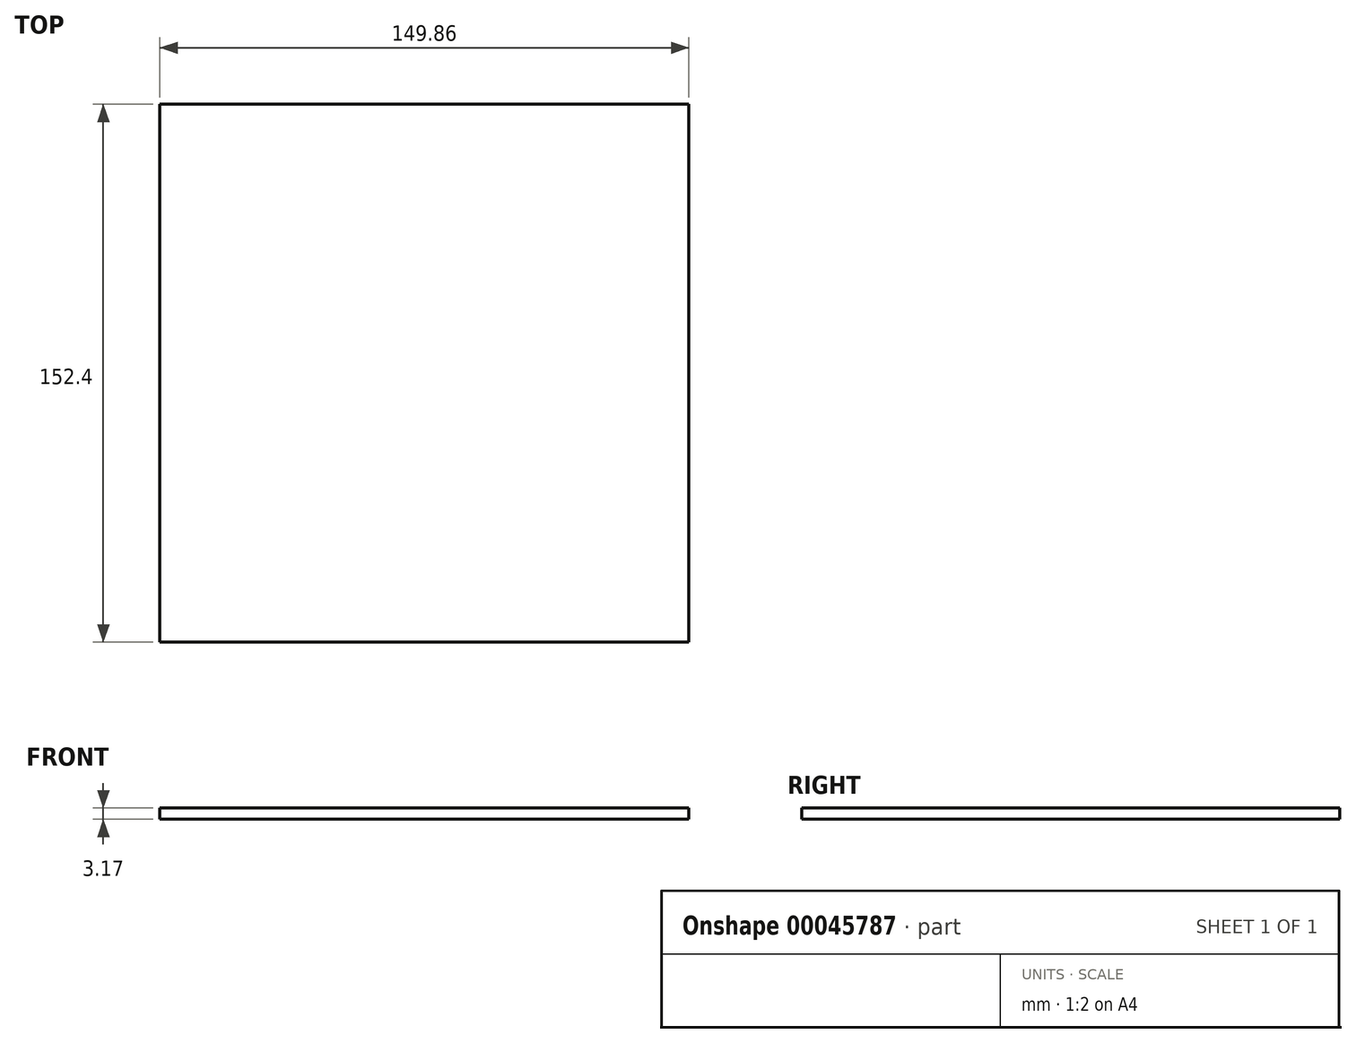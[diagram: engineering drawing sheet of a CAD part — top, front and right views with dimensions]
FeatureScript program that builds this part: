
annotation { "Feature Type Name" : "Feature", "Feature Type Description" : "" }
export const myFeature = defineFeature(function(context is Context, id is Id, definition is map)
    precondition{}
    {
        {
            var Q0;
            Q0=qCreatedBy(makeId("Top.planeOp"),FACE);
            var sketch = newSketch(context, id + "F0", { "sketchPlane" : qUnion([Q0])});
            skLineSegment(sketch, "E0.rect.bottom", {"start": v(-74.93, 76.2) * mm, "end": v(74.93, 76.2) * mm});
            skLineSegment(sketch, "E0.rect.top", {"start": v(-74.93, -76.2) * mm, "end": v(74.93, -76.2) * mm});
            skLineSegment(sketch, "E0.rect.left", {"start": v(-74.93, 76.2) * mm, "end": v(-74.93, -76.2) * mm});
            skLineSegment(sketch, "E0.rect.right", {"start": v(74.93, 76.2) * mm, "end": v(74.93, -76.2) * mm});
            skPoint(sketch, "E0.rect.middle", {"position": v(0, 0) * mm});
            skSolve(sketch);
        }
        {
            var Q0;
            Q0=makeQuery(id+"F0.imprint","IMPRINT",FACE,{"disambiguationData":[TD([[makeQuery(id+"F0.imprint","IMPRINT",EDGE,{"derivedFrom":sQuery(id+"F0.wireOp",EDGE,"E0.rect.bottom")}),-1.0]])]});
            extrude(context, id + "F1", {"entities" : qUnion([Q0]), "depth" : 3.17 * mm});
        }
    });
